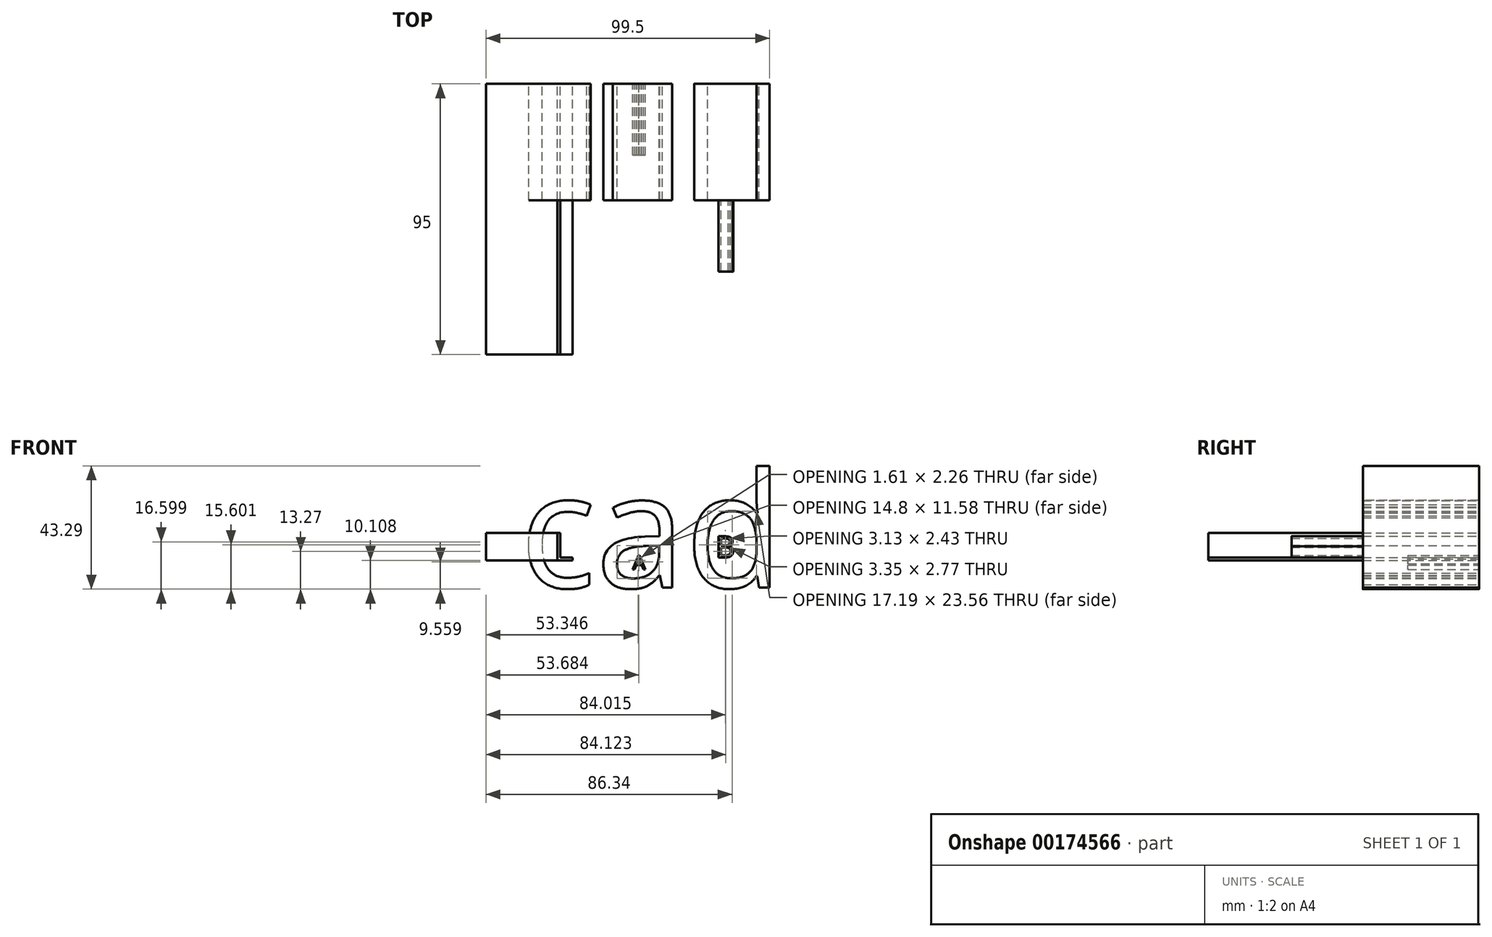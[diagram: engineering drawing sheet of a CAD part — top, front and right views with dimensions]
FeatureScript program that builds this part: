
annotation { "Feature Type Name" : "Feature", "Feature Type Description" : "" }
export const myFeature = defineFeature(function(context is Context, id is Id, definition is map)
    precondition{}
    {
        {
            var Q0;
            Q0=qCreatedBy(makeId("Front.planeOp"),FACE);
            var sketch = newSketch(context, id + "F0", { "sketchPlane" : qUnion([Q0])});
            skText(sketch, "E0", { "text": "cad", "fontName": "OpenSans-Regular.ttf"});
            const initialGuessF0  = {"E0": [-0.03218, 0, 1, 0, 0.0405]};
            skSetInitialGuess(sketch, initialGuessF0);
            skSolve(sketch);
        }
        {
            var Q0;
            Q0 = qSketchRegion(id + "F0", true);
            extrude(context, id + "F1", {"entities" : qUnion([Q0]), "depth" : 40.8 * mm});
        }
        {
            var Q0;
            Q0=qCreatedBy(makeId("Front.planeOp"),FACE);
            var sketch = newSketch(context, id + "F2", { "sketchPlane" : qUnion([Q0])});
            skText(sketch, "E1", { "text": "L", "fontName": "OpenSans-Regular.ttf"});
            const initialGuessF2  = {"E1": [-0.0203, 0.00952, 1, 0, 0.0097]};
            skSetInitialGuess(sketch, initialGuessF2);
            skSolve(sketch);
        }
        {
            var Q0;
            Q0=makeQuery(id+"F2.imprint","IMPRINT",FACE,{"disambiguationData":[TD([[makeQuery(id+"F2.imprint","IMPRINT",EDGE,{"derivedFrom":sQuery(id+"F2.wireOp",EDGE,"E1.sketch_text.stroke-0")}),-1.0]])]});
            extrude(context, id + "F3", {"entities" : qUnion([Q0]), "depth" : 25 * mm});
        }
        {
            var Q0;
            Q0=qCreatedBy(makeId("Front.planeOp"),FACE);
            var sketch = newSketch(context, id + "F4", { "sketchPlane" : qUnion([Q0])});
            skText(sketch, "E2", { "text": "A", "fontName": "OpenSans-Regular.ttf"});
            const initialGuessF4  = {"E2": [0.0075, 0.00633, 1, 0, 0.00501]};
            skSetInitialGuess(sketch, initialGuessF4);
            skSolve(sketch);
        }
        {
            var Q0;
            Q0=makeQuery(id+"F4.imprint","IMPRINT",FACE,{"disambiguationData":[TD([[makeQuery(id+"F4.imprint","IMPRINT",EDGE,{"derivedFrom":sQuery(id+"F4.wireOp",EDGE,"E2.sketch_text.stroke-0")}),-1.0]])]});
            extrude(context, id + "F5", {"entities" : qUnion([Q0]), "depth" : 25 * mm});
        }
        {
            var Q0;
            Q0=makeQuery(id+"F1.opExtrude","CAP_FACE",FACE,{"disambiguationData":[OSD([sQuery(id+"F0.wireOp",EDGE,"E0.sketch_text.stroke-15"),sQuery(id+"F0.wireOp",EDGE,"E0.sketch_text.stroke-16"),sQuery(id+"F0.wireOp",EDGE,"E0.sketch_text.stroke-17"),sQuery(id+"F0.wireOp",EDGE,"E0.sketch_text.stroke-18"),sQuery(id+"F0.wireOp",EDGE,"E0.sketch_text.stroke-19"),sQuery(id+"F0.wireOp",EDGE,"E0.sketch_text.stroke-20"),sQuery(id+"F0.wireOp",EDGE,"E0.sketch_text.stroke-21"),sQuery(id+"F0.wireOp",EDGE,"E0.sketch_text.stroke-22"),sQuery(id+"F0.wireOp",EDGE,"E0.sketch_text.stroke-23"),sQuery(id+"F0.wireOp",EDGE,"E0.sketch_text.stroke-24"),sQuery(id+"F0.wireOp",EDGE,"E0.sketch_text.stroke-25"),sQuery(id+"F0.wireOp",EDGE,"E0.sketch_text.stroke-26"),sQuery(id+"F0.wireOp",EDGE,"E0.sketch_text.stroke-27"),sQuery(id+"F0.wireOp",EDGE,"E0.sketch_text.stroke-28"),sQuery(id+"F0.wireOp",EDGE,"E0.sketch_text.stroke-29"),sQuery(id+"F0.wireOp",EDGE,"E0.sketch_text.stroke-30"),sQuery(id+"F0.wireOp",EDGE,"E0.sketch_text.stroke-31"),sQuery(id+"F0.wireOp",EDGE,"E0.sketch_text.stroke-32"),sQuery(id+"F0.wireOp",EDGE,"E0.sketch_text.stroke-33"),sQuery(id+"F0.wireOp",EDGE,"E0.sketch_text.stroke-34"),sQuery(id+"F0.wireOp",EDGE,"E0.sketch_text.stroke-35"),sQuery(id+"F0.wireOp",EDGE,"E0.sketch_text.stroke-36"),sQuery(id+"F0.wireOp",EDGE,"E0.sketch_text.stroke-37"),sQuery(id+"F0.wireOp",EDGE,"E0.sketch_text.stroke-38"),sQuery(id+"F0.wireOp",EDGE,"E0.sketch_text.stroke-39"),sQuery(id+"F0.wireOp",EDGE,"E0.sketch_text.stroke-40"),sQuery(id+"F0.wireOp",EDGE,"E0.sketch_text.stroke-41")])],"isStart":false});
            var sketch = newSketch(context, id + "F6", { "sketchPlane" : qUnion([Q0])});
            skText(sketch, "E3", { "text": "B", "fontName": "OpenSans-Regular.ttf"});
            const initialGuessF6  = {"E3": [0.03659, 0.0106, 1, 0, 0.00747]};
            skSetInitialGuess(sketch, initialGuessF6);
            skSolve(sketch);
        }
        {
            var Q0;
            Q0 = qSketchRegion(id + "F6", true);
            extrude(context, id + "F7", {"entities" : qUnion([Q0]), "depth" : 25 * mm});
        }
        {
            var Q0;
            Q0=makeQuery(id+"F3.opExtrude","CAP_FACE",FACE,{"disambiguationData":[OSD([sQuery(id+"F2.wireOp",EDGE,"E1.sketch_text.stroke-0"),sQuery(id+"F2.wireOp",EDGE,"E1.sketch_text.stroke-1"),sQuery(id+"F2.wireOp",EDGE,"E1.sketch_text.stroke-2"),sQuery(id+"F2.wireOp",EDGE,"E1.sketch_text.stroke-3"),sQuery(id+"F2.wireOp",EDGE,"E1.sketch_text.stroke-4"),sQuery(id+"F2.wireOp",EDGE,"E1.sketch_text.stroke-5")])],"isStart":false});
            extrude(context, id + "F8", {"entities" : qUnion([Q0]), "operationType" : NewBodyOperationType.ADD, "depth" : 30 * mm});
        }
        {
            var Q0;
            Q0=makeQuery(id+"F8.opExtrude","CAP_FACE",FACE,{"disambiguationData":[OSD([sQuery(id+"F2.wireOp",EDGE,"E1.sketch_text.stroke-0"),sQuery(id+"F2.wireOp",EDGE,"E1.sketch_text.stroke-1"),sQuery(id+"F2.wireOp",EDGE,"E1.sketch_text.stroke-2"),sQuery(id+"F2.wireOp",EDGE,"E1.sketch_text.stroke-3"),sQuery(id+"F2.wireOp",EDGE,"E1.sketch_text.stroke-4"),sQuery(id+"F2.wireOp",EDGE,"E1.sketch_text.stroke-5")])],"isStart":false});
            extrude(context, id + "F9", {"entities" : qUnion([Q0]), "operationType" : NewBodyOperationType.ADD, "depth" : 20 * mm});
        }
        {
            var Q0;
            Q0=makeQuery(id+"F9.opExtrude","CAP_FACE",FACE,{"disambiguationData":[OSD([sQuery(id+"F2.wireOp",EDGE,"E1.sketch_text.stroke-0"),sQuery(id+"F2.wireOp",EDGE,"E1.sketch_text.stroke-1"),sQuery(id+"F2.wireOp",EDGE,"E1.sketch_text.stroke-2"),sQuery(id+"F2.wireOp",EDGE,"E1.sketch_text.stroke-3"),sQuery(id+"F2.wireOp",EDGE,"E1.sketch_text.stroke-4"),sQuery(id+"F2.wireOp",EDGE,"E1.sketch_text.stroke-5")])],"isStart":false});
            extrude(context, id + "F10", {"entities" : qUnion([Q0]), "operationType" : NewBodyOperationType.ADD, "depth" : 20 * mm});
        }
        {
            var Q0;
            {var subQ0=sQuery(id+"F2.wireOp",EDGE,"E1.sketch_text.stroke-0");Q0=makeQuery(id+"F10.boolean.opBoolean","MERGE",FACE,{"derivedFrom":[makeQuery(id+"F9.boolean.opBoolean","MERGE",FACE,{"derivedFrom":[makeQuery(id+"F8.boolean.opBoolean","MERGE",FACE,{"derivedFrom":[makeQuery(id+"F3.opExtrude","SWEPT_FACE",FACE,{"disambiguationData":[OSD([subQ0])]}),makeQuery(id+"F8.opExtrude","SWEPT_FACE",FACE,{"disambiguationData":[OSD([subQ0])]})]}),makeQuery(id+"F9.opExtrude","SWEPT_FACE",FACE,{"disambiguationData":[OSD([subQ0])]})]}),makeQuery(id+"F10.opExtrude","SWEPT_FACE",FACE,{"disambiguationData":[OSD([subQ0])]})]});}
            extrude(context, id + "F11", {"entities" : qUnion([Q0]), "depth" : 25 * mm});
        }
    });
